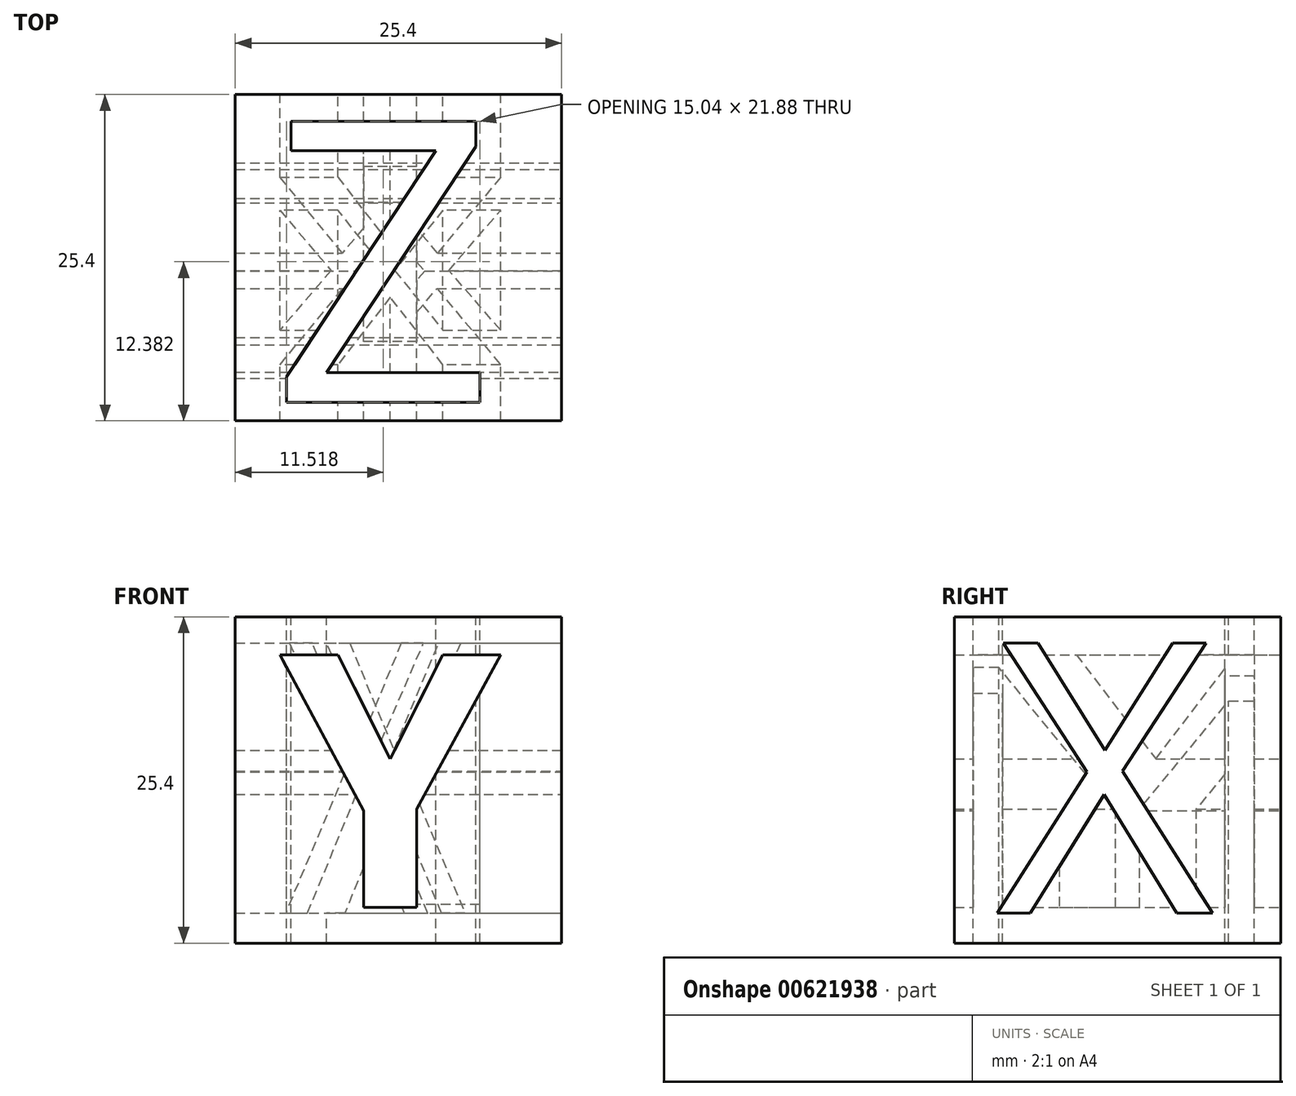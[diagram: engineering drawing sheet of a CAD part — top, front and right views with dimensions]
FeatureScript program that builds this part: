
annotation { "Feature Type Name" : "Feature", "Feature Type Description" : "" }
export const myFeature = defineFeature(function(context is Context, id is Id, definition is map)
    precondition{}
    {
        {
            var Q0;
            Q0=qCreatedBy(makeId("Front.planeOp"),FACE);
            var sketch = newSketch(context, id + "F0", { "sketchPlane" : qUnion([Q0])});
            skLineSegment(sketch, "E0.bottom", {"start": v(-12.7, -12.7) * mm, "end": v(12.7, -12.7) * mm});
            skLineSegment(sketch, "E0.top", {"start": v(-12.7, 12.7) * mm, "end": v(12.7, 12.7) * mm});
            skLineSegment(sketch, "E0.left", {"start": v(-12.7, -12.7) * mm, "end": v(-12.7, 12.7) * mm});
            skLineSegment(sketch, "E0.right", {"start": v(12.7, -12.7) * mm, "end": v(12.7, 12.7) * mm});
            skPoint(sketch, "E0.middle", {"position": v(0, 0) * mm});
            skText(sketch, "E1", { "text": "Y", "fontName": "OpenSans-Bold.ttf"});
            const initialGuessF0  = {"E1": [-0.00923, -0.00992, 1, 0, 0.01983]};
            skSetInitialGuess(sketch, initialGuessF0);
            skSolve(sketch);
        }
        {
            var Q0;
            Q0 = qSketchRegion(id + "F0", true);
            extrude(context, id + "F1", {"entities" : qUnion([Q0]), "endBound" : BoundingType.SYMMETRIC, "depth" : 25.4 * mm, "offsetDistance" : 25.4 * mm});
        }
        {
            var Q0;
            Q0=qCreatedBy(makeId("Right.planeOp"),FACE);
            var sketch = newSketch(context, id + "F2", { "sketchPlane" : qUnion([Q0])});
            skText(sketch, "E2", { "text": "X", "fontName": "OpenSans-Regular.ttf"});
            const initialGuessF2  = {"E2": [-0.0095, -0.01037, 1, 0, 0.02119]};
            skSetInitialGuess(sketch, initialGuessF2);
            skSolve(sketch);
        }
        {
            var Q0;
            Q0 = qSketchRegion(id + "F2", true);
            extrude(context, id + "F3", {"entities" : qUnion([Q0]), "operationType" : NewBodyOperationType.REMOVE, "endBound" : BoundingType.SYMMETRIC, "oppositeDirection" : true, "depth" : 25.4 * mm, "offsetDistance" : 25.4 * mm});
        }
        {
            var Q0;
            Q0=qCreatedBy(makeId("Top.planeOp"),FACE);
            var sketch = newSketch(context, id + "F4", { "sketchPlane" : qUnion([Q0])});
            skText(sketch, "E3", { "text": "Z", "fontName": "OpenSans-Regular.ttf"});
            const initialGuessF4  = {"E3": [-0.00993, -0.01126, 1, 0, 0.02207]};
            skSetInitialGuess(sketch, initialGuessF4);
            skSolve(sketch);
        }
        {
            var Q0;
            Q0 = qSketchRegion(id + "F4", true);
            extrude(context, id + "F5", {"entities" : qUnion([Q0]), "operationType" : NewBodyOperationType.REMOVE, "endBound" : BoundingType.SYMMETRIC, "oppositeDirection" : true, "depth" : 25.4 * mm, "offsetDistance" : 25.4 * mm});
        }
        {
            var Q0;
            Q0=makeQuery(id+"F5.boolean.opBoolean","SPLIT",BODY,{"disambiguationData":[OD(0.0)],"derivedFrom":makeQuery(id+"F1.opExtrude","SWEPT_BODY",BODY,{"disambiguationData":[OSD([sQuery(id+"F0.wireOp",EDGE,"E0.bottom"),sQuery(id+"F0.wireOp",EDGE,"E0.top"),sQuery(id+"F0.wireOp",EDGE,"E0.left"),sQuery(id+"F0.wireOp",EDGE,"E0.right"),sQuery(id+"F0.wireOp",EDGE,"E1.sketch_text.stroke-0"),sQuery(id+"F0.wireOp",EDGE,"E1.sketch_text.stroke-1"),sQuery(id+"F0.wireOp",EDGE,"E1.sketch_text.stroke-2"),sQuery(id+"F0.wireOp",EDGE,"E1.sketch_text.stroke-3"),sQuery(id+"F0.wireOp",EDGE,"E1.sketch_text.stroke-4"),sQuery(id+"F0.wireOp",EDGE,"E1.sketch_text.stroke-5"),sQuery(id+"F0.wireOp",EDGE,"E1.sketch_text.stroke-6"),sQuery(id+"F0.wireOp",EDGE,"E1.sketch_text.stroke-7"),sQuery(id+"F0.wireOp",EDGE,"E1.sketch_text.stroke-8")])]})});
            deleteBodies(context, id + "F6", {"entities" : qUnion([Q0])});
        }
    });
